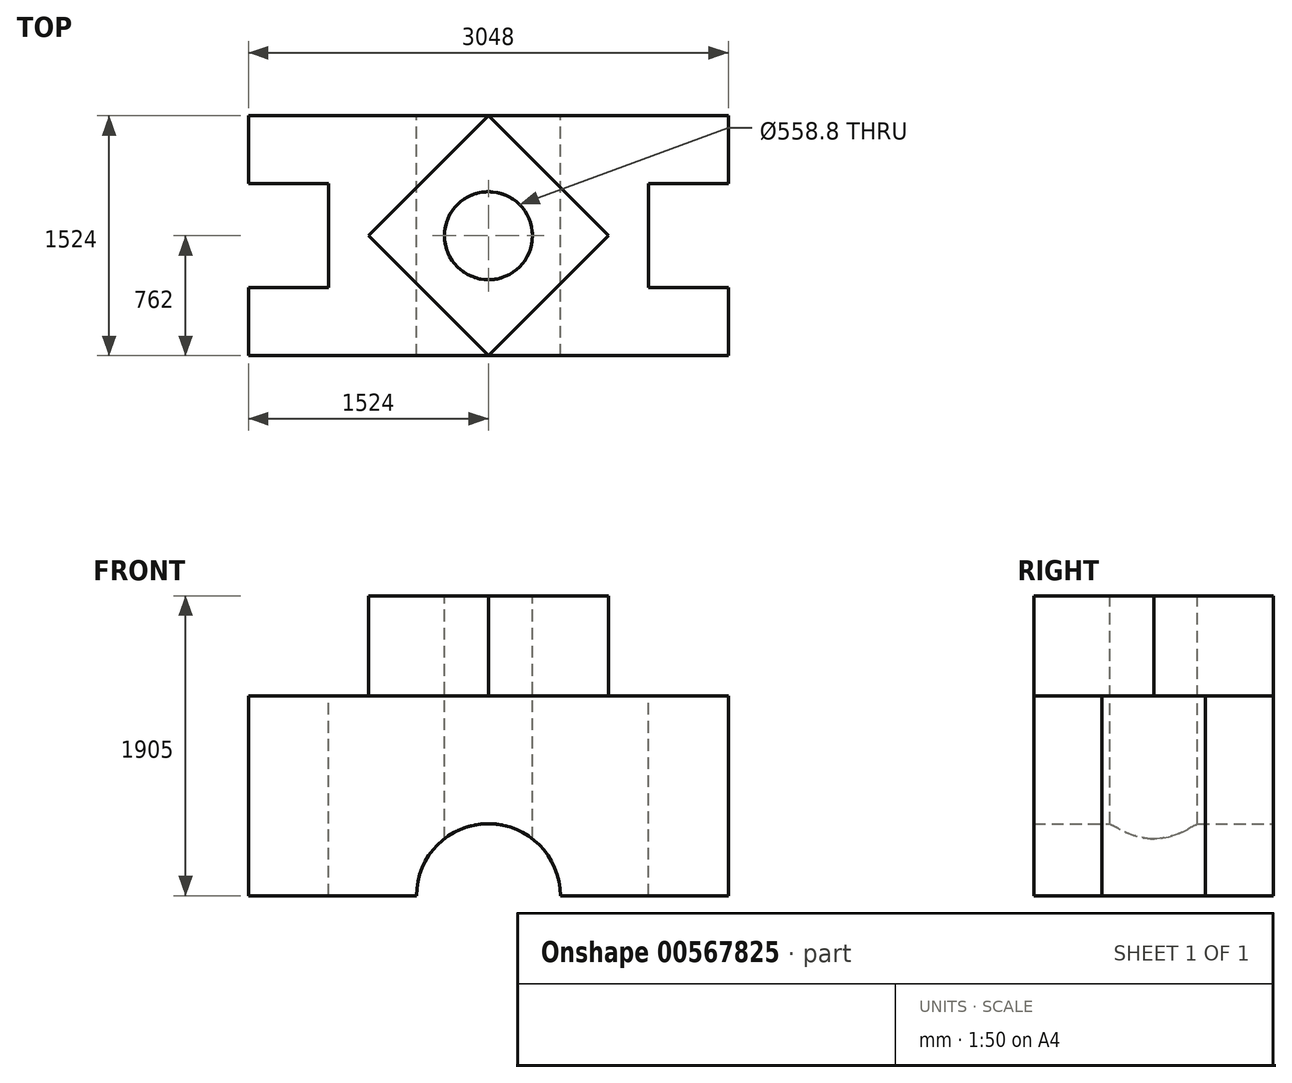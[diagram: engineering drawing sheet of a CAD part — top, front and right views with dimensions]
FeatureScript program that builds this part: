
annotation { "Feature Type Name" : "Feature", "Feature Type Description" : "" }
export const myFeature = defineFeature(function(context is Context, id is Id, definition is map)
    precondition{}
    {
        {
            var Q0;
            Q0=qCreatedBy(makeId("Front.planeOp"),FACE);
            var sketch = newSketch(context, id + "F0", { "sketchPlane" : qUnion([Q0])});
            skLineSegment(sketch, "E0.bottom", {"start": v(-1524, -635) * mm, "end": v(-457.2, -635) * mm});
            skLineSegment(sketch, "E0.top", {"start": v(-1524, 635) * mm, "end": v(1524, 635) * mm});
            skLineSegment(sketch, "E0.left", {"start": v(-1524, -635) * mm, "end": v(-1524, 635) * mm});
            skLineSegment(sketch, "E0.right", {"start": v(1524, -635) * mm, "end": v(1524, 635) * mm});
            skPoint(sketch, "E0.middle", {"position": v(0, 0) * mm});
            skArc(sketch, "E1", {"start": v(457.2, -635) * mm, "mid": v(0, -177.8) * mm, "end": v(-457.2, -635) * mm});
            skLineSegment(sketch, "E2.trimOffspring", {"start": v(457.2, -635) * mm, "end": v(1524, -635) * mm});
            skSolve(sketch);
        }
        {
            var Q0;
            Q0 = qSketchRegion(id + "F0", true);
            extrude(context, id + "F1", {"entities" : qUnion([Q0]), "depth" : 1524 * mm, "offsetDistance" : 25.4 * mm});
        }
        {
            var Q0;
            Q0=makeQuery(id+"F1.opExtrude","SWEPT_FACE",FACE,{"disambiguationData":[OSD([sQuery(id+"F0.wireOp",EDGE,"E0.top")])]});
            var sketch = newSketch(context, id + "F2", { "sketchPlane" : qUnion([Q0])});
            skLineSegment(sketch, "E3", {"start": v(-1524, 0) * mm, "end": v(-1524, -431.8) * mm});
            skLineSegment(sketch, "E4", {"start": v(-1524, -431.8) * mm, "end": v(-1524, -1092.2) * mm});
            skLineSegment(sketch, "E5", {"start": v(-1524, -1092.2) * mm, "end": v(-1524, -1524) * mm});
            skLineSegment(sketch, "E6", {"start": v(1524, 0) * mm, "end": v(1524, -431.8) * mm});
            skLineSegment(sketch, "E7", {"start": v(1524, -431.8) * mm, "end": v(1524, -1092.2) * mm});
            skLineSegment(sketch, "E8", {"start": v(1524, -1092.2) * mm, "end": v(1524, -1524) * mm});
            skLineSegment(sketch, "E9", {"start": v(-1524, -431.8) * mm, "end": v(-1016, -431.8) * mm});
            skLineSegment(sketch, "E10", {"start": v(-1016, -431.8) * mm, "end": v(-1016, -1092.2) * mm});
            skLineSegment(sketch, "E11", {"start": v(-1016, -1092.2) * mm, "end": v(-1524, -1092.2) * mm});
            skLineSegment(sketch, "E12", {"start": v(1524, -431.8) * mm, "end": v(1016, -431.8) * mm});
            skLineSegment(sketch, "E13", {"start": v(1016, -431.8) * mm, "end": v(1016, -1092.2) * mm});
            skLineSegment(sketch, "E14", {"start": v(1016, -1092.2) * mm, "end": v(1524, -1092.2) * mm});
            skSolve(sketch);
        }
        {
            var Q0;
            Q0 = qSketchRegion(id + "F2", true);
            extrude(context, id + "F3", {"entities" : qUnion([Q0]), "operationType" : NewBodyOperationType.ADD, "depth" : 25.4 * mm, "offsetDistance" : 25.4 * mm});
        }
        {
            var Q0;
            Q0=makeQuery(id+"F3.opExtrude","CAP_FACE",FACE,{"disambiguationData":[OSD([sQuery(id+"F2.wireOp",EDGE,"E4"),sQuery(id+"F2.wireOp",EDGE,"E9"),sQuery(id+"F2.wireOp",EDGE,"E10"),sQuery(id+"F2.wireOp",EDGE,"E11")])],"isStart":false});
            var Q1;
            Q1=makeQuery(id+"F3.opExtrude","CAP_FACE",FACE,{"disambiguationData":[OSD([sQuery(id+"F2.wireOp",EDGE,"E7"),sQuery(id+"F2.wireOp",EDGE,"E12"),sQuery(id+"F2.wireOp",EDGE,"E13"),sQuery(id+"F2.wireOp",EDGE,"E14")])],"isStart":false});
            extrude(context, id + "F4", {"entities" : qUnion([Q0, Q1]), "operationType" : NewBodyOperationType.REMOVE, "endBound" : BoundingType.THROUGH_ALL, "oppositeDirection" : true, "depth" : 25.4 * mm, "offsetDistance" : 25.4 * mm});
        }
        {
            var Q0;
            Q0=makeQuery(id+"F1.opExtrude","SWEPT_FACE",FACE,{"disambiguationData":[OSD([sQuery(id+"F0.wireOp",EDGE,"E0.top")])]});
            var sketch = newSketch(context, id + "F5", { "sketchPlane" : qUnion([Q0])});
            skPoint(sketch, "E15.endSnap0", {"position": v(-1016, -762) * mm});
            skPoint(sketch, "E15.end.orphan", {"position": v(-762, -762) * mm});
            skPoint(sketch, "E15.start.orphan", {"position": v(0, 0) * mm});
            skLineSegment(sketch, "E16", {"start": v(0, 0) * mm, "end": v(-762, -762) * mm});
            skLineSegment(sketch, "E17", {"start": v(-762, -762) * mm, "end": v(0, -1524) * mm});
            skLineSegment(sketch, "E18", {"start": v(0, -1524) * mm, "end": v(762, -762) * mm});
            skLineSegment(sketch, "E19", {"start": v(762, -762) * mm, "end": v(0, 0) * mm});
            skLineSegment(sketch, "E20", {"start": v(-1016, -762) * mm, "end": v(-762, -762) * mm});
            skLineSegment(sketch, "E21", {"start": v(762, -762) * mm, "end": v(1016, -762) * mm});
            skSolve(sketch);
        }
        {
            var Q0;
            Q0=makeQuery(id+"F5.imprint","IMPRINT",FACE,{"disambiguationData":[TD([[makeQuery(id+"F5.imprint","IMPRINT",EDGE,{"derivedFrom":sQuery(id+"F5.wireOp",EDGE,"E16")}),1.0]])]});
            extrude(context, id + "F6", {"entities" : qUnion([Q0]), "operationType" : NewBodyOperationType.ADD, "depth" : 635 * mm, "offsetDistance" : 25.4 * mm});
        }
        {
            var Q0;
            Q0=makeQuery(id+"F6.opExtrude","CAP_FACE",FACE,{"disambiguationData":[OSD([sQuery(id+"F5.wireOp",EDGE,"E16"),sQuery(id+"F5.wireOp",EDGE,"E17"),sQuery(id+"F5.wireOp",EDGE,"E18"),sQuery(id+"F5.wireOp",EDGE,"E19")])],"isStart":false});
            var sketch = newSketch(context, id + "F7", { "sketchPlane" : qUnion([Q0])});
            skCircle(sketch, "E22", {"center": v(0, -762) * mm, "radius": 279.4 * mm});
            skSolve(sketch);
        }
        {
            var Q0;
            Q0=makeQuery(id+"F7.imprint","IMPRINT",FACE,{"disambiguationData":[TD([[makeQuery(id+"F7.imprint","IMPRINT",EDGE,{"derivedFrom":sQuery(id+"F7.wireOp",EDGE,"E22")}),1.0]])]});
            extrude(context, id + "F8", {"entities" : qUnion([Q0]), "operationType" : NewBodyOperationType.REMOVE, "endBound" : BoundingType.THROUGH_ALL, "oppositeDirection" : true, "depth" : 25.4 * mm, "offsetDistance" : 25.4 * mm});
        }
    });
